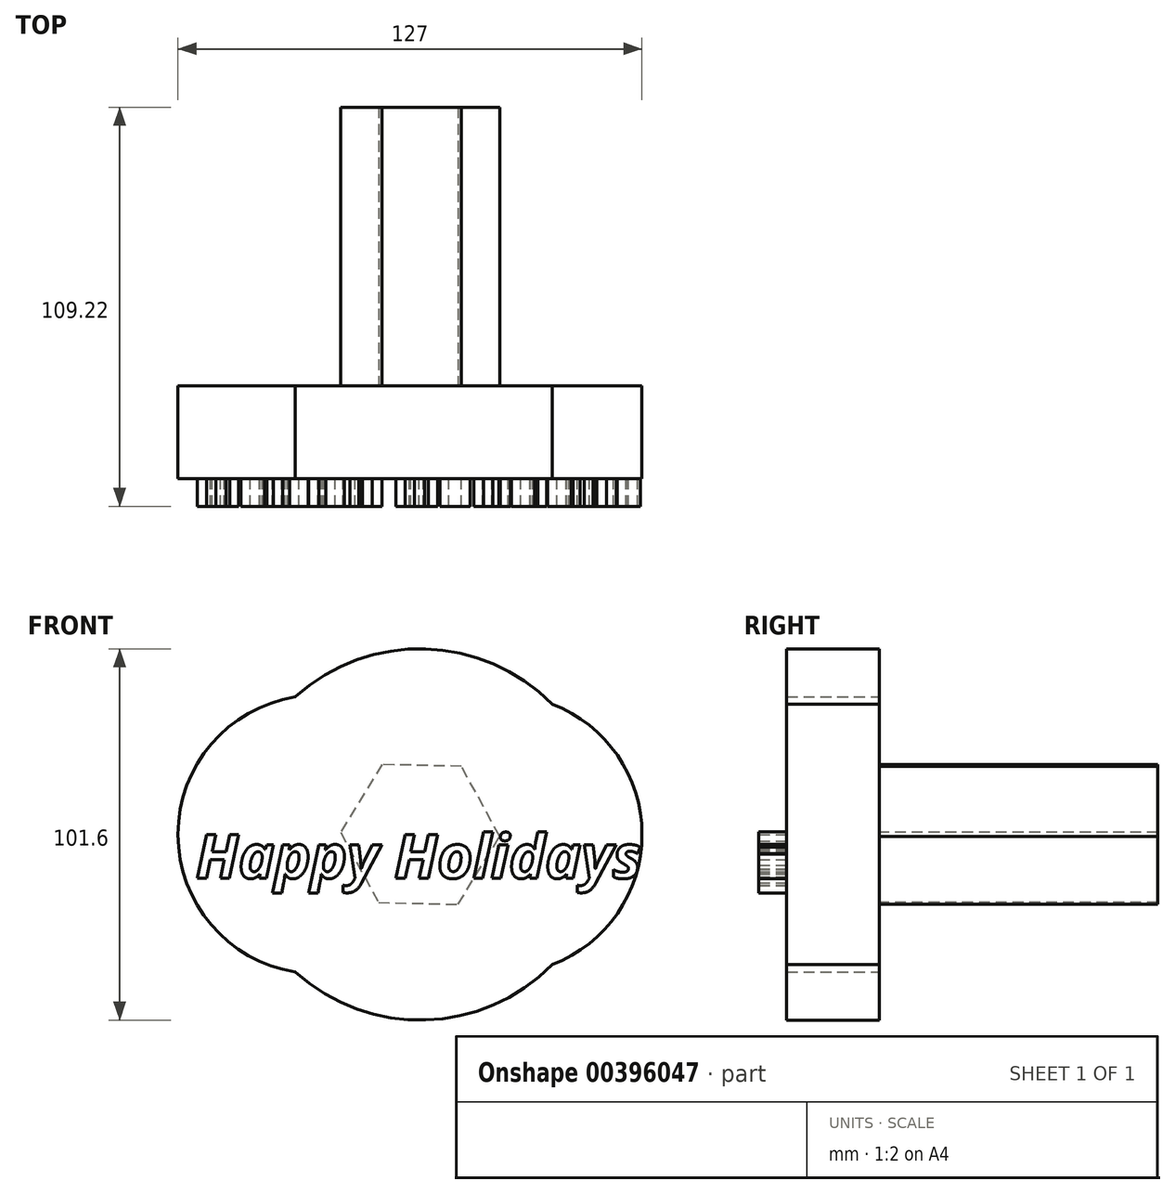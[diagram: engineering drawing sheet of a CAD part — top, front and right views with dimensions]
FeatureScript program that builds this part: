
annotation { "Feature Type Name" : "Feature", "Feature Type Description" : "" }
export const myFeature = defineFeature(function(context is Context, id is Id, definition is map)
    precondition{}
    {
        {
            var Q0;
            Q0=qCreatedBy(makeId("Front.planeOp"),FACE);
            var sketch = newSketch(context, id + "F0", { "sketchPlane" : qUnion([Q0])});
            skCircle(sketch, "E0", {"center": v(22.66, 0) * mm, "radius": 38.1 * mm});
            skCircle(sketch, "E1", {"center": v(-28.14, 0) * mm, "radius": 38.1 * mm});
            skCircle(sketch, "E2", {"center": v(0, 0) * mm, "radius": 50.8 * mm});
            skSolve(sketch);
        }
        {
            var Q0;
            {var subQ0=sQuery(id+"F0.wireOp",EDGE,"E2");var subQ1=sQuery(id+"F0.wireOp",EDGE,"E0");var subQ2=makeQuery(id+"F0.imprint","INTERSECT",VERTEX,{"disambiguationData":[OD(0.0)],"derivedFrom":[subQ1,subQ0]});Q0=makeQuery(id+"F0.imprint","IMPRINT",FACE,{"disambiguationData":[TD([[makeQuery(id+"F0.imprint","IMPRINT",EDGE,{"disambiguationData":[TD([[subQ2,1.0]])],"derivedFrom":subQ1}),1.0]])]});}
            var Q1;
            {var subQ0=sQuery(id+"F0.wireOp",EDGE,"E2");var subQ1=sQuery(id+"F0.wireOp",EDGE,"E1");var subQ2=makeQuery(id+"F0.imprint","INTERSECT",VERTEX,{"disambiguationData":[OD(0.0)],"derivedFrom":[subQ1,subQ0]});Q1=makeQuery(id+"F0.imprint","IMPRINT",FACE,{"disambiguationData":[TD([[makeQuery(id+"F0.imprint","IMPRINT",EDGE,{"disambiguationData":[TD([[subQ2,-1.0]])],"derivedFrom":subQ1}),1.0]])]});}
            var Q2;
            {var subQ0=sQuery(id+"F0.wireOp",EDGE,"E2");var subQ1=sQuery(id+"F0.wireOp",EDGE,"E0");var subQ2=makeQuery(id+"F0.imprint","INTERSECT",VERTEX,{"disambiguationData":[OD(0.0)],"derivedFrom":[subQ1,subQ0]});Q2=makeQuery(id+"F0.imprint","IMPRINT",FACE,{"disambiguationData":[TD([[makeQuery(id+"F0.imprint","IMPRINT",EDGE,{"disambiguationData":[TD([[subQ2,-1.0]])],"derivedFrom":subQ1}),-1.0]])]});}
            var Q3;
            {var subQ0=sQuery(id+"F0.wireOp",EDGE,"E2");var subQ1=sQuery(id+"F0.wireOp",EDGE,"E0");var subQ2=makeQuery(id+"F0.imprint","INTERSECT",VERTEX,{"disambiguationData":[OD(1.0)],"derivedFrom":[subQ1,subQ0]});Q3=makeQuery(id+"F0.imprint","IMPRINT",FACE,{"disambiguationData":[TD([[makeQuery(id+"F0.imprint","IMPRINT",EDGE,{"disambiguationData":[TD([[subQ2,1.0]])],"derivedFrom":subQ1}),-1.0]])]});}
            var Q4;
            {var subQ0=sQuery(id+"F0.wireOp",EDGE,"E2");var subQ1=sQuery(id+"F0.wireOp",EDGE,"E0");var subQ2=makeQuery(id+"F0.imprint","INTERSECT",VERTEX,{"disambiguationData":[OD(0.0)],"derivedFrom":[subQ1,subQ0]});Q4=makeQuery(id+"F0.imprint","IMPRINT",FACE,{"disambiguationData":[TD([[makeQuery(id+"F0.imprint","IMPRINT",EDGE,{"disambiguationData":[TD([[subQ2,-1.0]])],"derivedFrom":subQ1}),1.0]])]});}
            var Q5;
            {var subQ0=sQuery(id+"F0.wireOp",EDGE,"E1");var subQ1=sQuery(id+"F0.wireOp",EDGE,"E0");var subQ2=makeQuery(id+"F0.imprint","INTERSECT",VERTEX,{"disambiguationData":[OD(0.0)],"derivedFrom":[subQ1,subQ0]});Q5=makeQuery(id+"F0.imprint","IMPRINT",FACE,{"disambiguationData":[TD([[makeQuery(id+"F0.imprint","IMPRINT",EDGE,{"disambiguationData":[TD([[subQ2,-1.0]])],"derivedFrom":subQ1}),-1.0]])]});}
            var Q6;
            {var subQ0=sQuery(id+"F0.wireOp",EDGE,"E1");var subQ1=sQuery(id+"F0.wireOp",EDGE,"E0");var subQ2=makeQuery(id+"F0.imprint","INTERSECT",VERTEX,{"disambiguationData":[OD(0.0)],"derivedFrom":[subQ1,subQ0]});Q6=makeQuery(id+"F0.imprint","IMPRINT",FACE,{"disambiguationData":[TD([[makeQuery(id+"F0.imprint","IMPRINT",EDGE,{"disambiguationData":[TD([[subQ2,-1.0]])],"derivedFrom":subQ1}),1.0]])]});}
            extrude(context, id + "F1", {"entities" : qUnion([Q0, Q1, Q2, Q3, Q4, Q5, Q6]), "depth" : 25.4 * mm});
        }
        {
            var Q0;
            Q0=makeQuery(id+"F1.opExtrude","CAP_FACE",FACE,{"disambiguationData":[OSD([sQuery(id+"F0.wireOp",EDGE,"E0"),sQuery(id+"F0.wireOp",EDGE,"E1"),sQuery(id+"F0.wireOp",EDGE,"E2")])],"isStart":true});
            var sketch = newSketch(context, id + "F2", { "sketchPlane" : qUnion([Q0])});
            skCircle(sketch, "E3.cCircle", {"center": v(0, 0) * mm, "radius": 18.87 * mm, "construction": true});
            skLineSegment(sketch, "E3.0", {"start": v(10.44, 19.13) * mm, "end": v(21.79, 0.52) * mm});
            skLineSegment(sketch, "E3.1", {"start": v(21.79, 0.52) * mm, "end": v(11.35, -18.6) * mm});
            skLineSegment(sketch, "E3.2", {"start": v(11.35, -18.6) * mm, "end": v(-10.44, -19.13) * mm});
            skLineSegment(sketch, "E3.3", {"start": v(-10.44, -19.13) * mm, "end": v(-21.79, -0.52) * mm});
            skLineSegment(sketch, "E3.4", {"start": v(-21.79, -0.52) * mm, "end": v(-11.35, 18.6) * mm});
            skLineSegment(sketch, "E3.5", {"start": v(-11.35, 18.6) * mm, "end": v(10.44, 19.13) * mm});
            skPoint(sketch, "E3.0.midPoint", {"position": v(16.11, 9.83) * mm});
            skSolve(sketch);
        }
        {
            var Q0;
            Q0 = qSketchRegion(id + "F2", true);
            extrude(context, id + "F3", {"entities" : qUnion([Q0]), "operationType" : NewBodyOperationType.ADD, "depth" : 76.2 * mm});
        }
        {
            var Q0;
            Q0=makeQuery(id+"F1.opExtrude","CAP_FACE",FACE,{"disambiguationData":[OSD([sQuery(id+"F0.wireOp",EDGE,"E0"),sQuery(id+"F0.wireOp",EDGE,"E1"),sQuery(id+"F0.wireOp",EDGE,"E2")])],"isStart":false});
            var sketch = newSketch(context, id + "F4", { "sketchPlane" : qUnion([Q0])});
            skText(sketch, "E4", { "text": "Happy Holidays", "fontName": "OpenSans-BoldItalic.ttf"});
            const initialGuessF4  = {"E4": [-0.06138, -0.012, 1, 0, 0.012]};
            skSetInitialGuess(sketch, initialGuessF4);
            skSolve(sketch);
        }
        {
            var Q0;
            Q0 = qSketchRegion(id + "F4", true);
            extrude(context, id + "F5", {"entities" : qUnion([Q0]), "operationType" : NewBodyOperationType.ADD, "depth" : 7.62 * mm});
        }
    });
